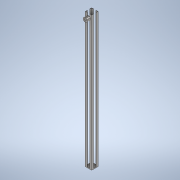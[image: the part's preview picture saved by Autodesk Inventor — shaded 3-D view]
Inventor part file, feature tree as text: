
AUTODESK INVENTOR PART (.ipt)
format: ipt  version: 2020 (Build 240168000, 168)  size: 164,352 bytes
history: native  units: mm
features: extrude x6, sketch x6
ambient origin geometry x8: Origin, YZ Plane, XZ Plane, XY Plane, X Axis, Y Axis, Z Axis, Center Point
bodies: Solid1 (feature_tree)
feature tree (12):
  extrude  "Extrusion1"  Depth=38.0mm
  extrude  "Extrusion5"  Depth=800.0mm TaperAngle=0.0deg
  sketch  "Sketch6"  dims[d20=15.0mm d21=55.0mm]
  extrude  "Extrusion6"  Depth=15.0mm
  extrude  "Extrusion7"  Depth=15.0mm
  extrude  "Extrusion8"  Depth=35.0mm
  extrude  "Extrusion9"  Depth=800.0mm TaperAngle=0.0deg
  sketch  "Sketch1"  dims[d0=38.0mm d1=38.0mm]
  sketch  "Sketch5"  dims[d2=5.0mm d3=0.0mm d18=800.0mm d19=0.0mm]
  sketch  "Sketch7"  dims[d22=55.0mm d23=15.0mm]
  sketch  "Sketch8"  dims[d24=35.0mm d25=35.0mm]
  sketch  "Sketch9"  dims[d26=800.0mm d27=0.0mm d28=800.0mm d29=0.0mm d30=10.0mm d31=2.0mm d32=0.0mm d33=13.0mm d34=20.0mm d35=0.0mm]
